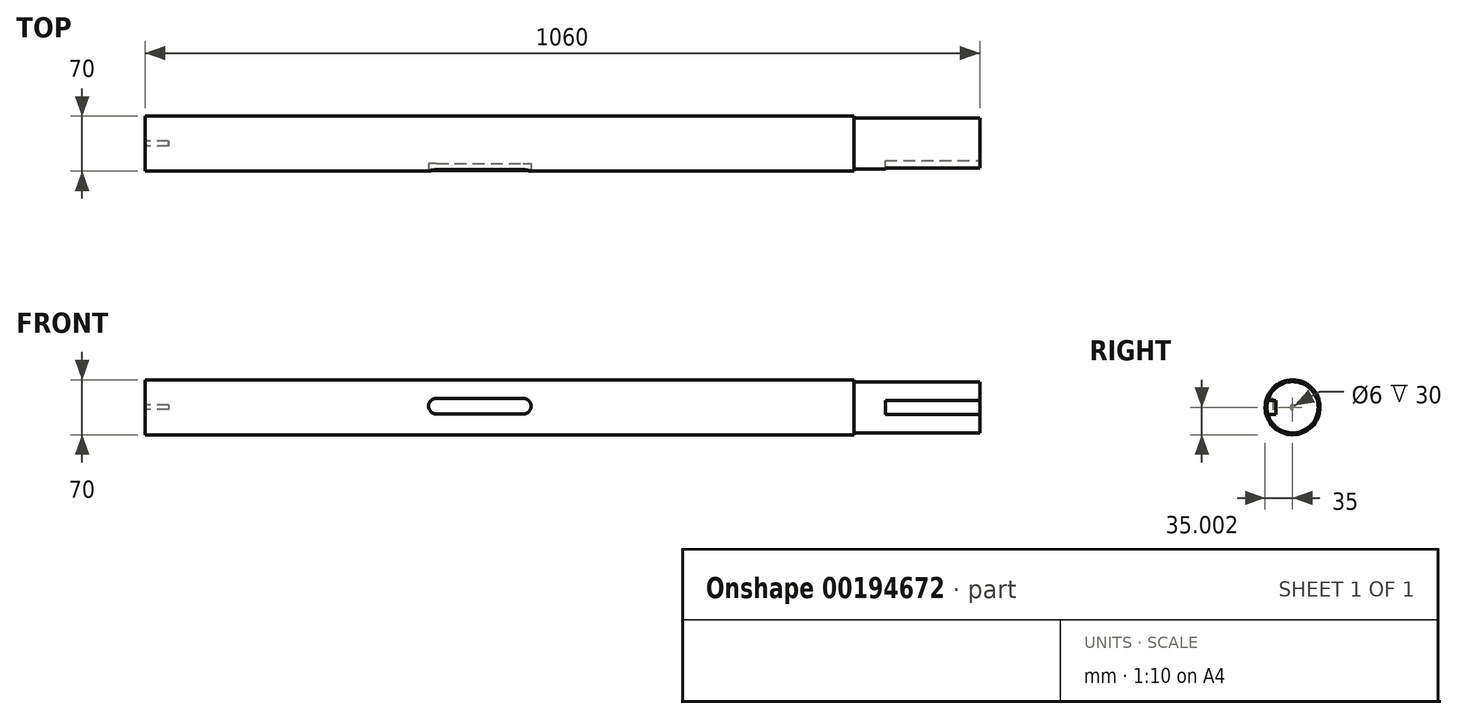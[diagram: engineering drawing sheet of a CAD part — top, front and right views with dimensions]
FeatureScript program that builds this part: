
annotation { "Feature Type Name" : "Feature", "Feature Type Description" : "" }
export const myFeature = defineFeature(function(context is Context, id is Id, definition is map)
    precondition{}
    {
        {
            var Q0;
            Q0=qCreatedBy(makeId("Front.planeOp"),FACE);
            var sketch = newSketch(context, id + "F0", { "sketchPlane" : qUnion([Q0])});
            skLineSegment(sketch, "E0", {"start": v(-663.35, -62.58) * mm, "end": v(236.65, -62.58) * mm});
            skLineSegment(sketch, "E1", {"start": v(236.65, -62.58) * mm, "end": v(236.65, -65.08) * mm});
            skLineSegment(sketch, "E2", {"start": v(236.65, -65.08) * mm, "end": v(396.65, -65.08) * mm});
            skLineSegment(sketch, "E3", {"start": v(396.65, -65.08) * mm, "end": v(396.65, -97.58) * mm});
            skLineSegment(sketch, "E4", {"start": v(396.65, -97.58) * mm, "end": v(-663.35, -97.58) * mm});
            skLineSegment(sketch, "E5", {"start": v(-663.35, -97.58) * mm, "end": v(-663.35, -62.58) * mm});
            skSolve(sketch);
        }
        {
            var Q0;
            Q0=makeQuery(id+"F0.imprint","IMPRINT",FACE,{"disambiguationData":[TD([[makeQuery(id+"F0.imprint","IMPRINT",EDGE,{"derivedFrom":sQuery(id+"F0.wireOp",EDGE,"E0")}),-1.0]])]});
            var Q1;
            Q1=sQuery(id+"F0.wireOp",EDGE,"E4");
            revolve(context, id + "F1", {"entities" : qUnion([Q0]), "axis" : qUnion([Q1]), "revolveType" : RevolveType.FULL});
        }
        {
            var Q0;
            Q0=makeQuery(id+"F1.opRevolve","SWEPT_FACE",FACE,{"disambiguationData":[OSD([sQuery(id+"F0.wireOp",EDGE,"E3")])]});
            var sketch = newSketch(context, id + "F2", { "sketchPlane" : qUnion([Q0])});
            skLineSegment(sketch, "E6", {"start": v(-31.23, -88.58) * mm, "end": v(-21.23, -88.58) * mm});
            skLineSegment(sketch, "E7", {"start": v(-21.23, -88.58) * mm, "end": v(-21.23, -106.58) * mm});
            skLineSegment(sketch, "E8", {"start": v(-21.23, -106.58) * mm, "end": v(-31.23, -106.58) * mm});
            skSolve(sketch);
        }
        {
            var Q0;
            {var subQ0=sQuery(id+"F2.wireOp",EDGE,"E6");Q0=makeQuery(id+"F2.imprint","IMPRINT",FACE,{"disambiguationData":[TD([[makeQuery(id+"F2.imprint","IMPRINT",EDGE,{"derivedFrom":subQ0}),-1.0]])]});}
            extrude(context, id + "F3", {"entities" : qUnion([Q0]), "operationType" : NewBodyOperationType.REMOVE, "oppositeDirection" : true, "depth" : 120 * mm});
        }
        {
            var Q0;
            Q0=qCreatedBy(makeId("Front.planeOp"),FACE);
            cPlane(context, id + "F4", {"entities" : qUnion([Q0]), "cplaneType" : CPlaneType.OFFSET, "offset" : 35 * mm, "width" : 150 * mm, "height" : 150 * mm});
        }
        {
            var Q0;
            Q0=qCreatedBy(id+"F4.planeOp",FACE);
            var sketch = newSketch(context, id + "F5", { "sketchPlane" : qUnion([Q0])});
            skLineSegment(sketch, "E9", {"start": v(-293.35, -86.1) * mm, "end": v(-183.35, -86.1) * mm});
            skLineSegment(sketch, "E10", {"start": v(-183.35, -106.1) * mm, "end": v(-293.35, -106.1) * mm});
            skArc(sketch, "E11", {"start": v(-293.35, -86.1) * mm, "mid": v(-303.35, -96.1) * mm, "end": v(-293.35, -106.1) * mm});
            skArc(sketch, "E12", {"start": v(-183.35, -106.1) * mm, "mid": v(-173.35, -96.1) * mm, "end": v(-183.35, -86.1) * mm});
            skSolve(sketch);
        }
        {
            var Q0;
            Q0=makeQuery(id+"F5.imprint","IMPRINT",FACE,{"disambiguationData":[TD([[makeQuery(id+"F5.imprint","IMPRINT",EDGE,{"derivedFrom":sQuery(id+"F5.wireOp",EDGE,"E9")}),-1.0]])]});
            extrude(context, id + "F6", {"entities" : qUnion([Q0]), "operationType" : NewBodyOperationType.REMOVE, "oppositeDirection" : true, "depth" : 10 * mm});
        }
        {
            var Q0;
            Q0=makeQuery(id+"F1.opRevolve","SWEPT_FACE",FACE,{"disambiguationData":[OSD([sQuery(id+"F0.wireOp",EDGE,"E5")])]});
            var sketch = newSketch(context, id + "F7", { "sketchPlane" : qUnion([Q0])});
            skCircle(sketch, "E13", {"center": v(0, -97.58) * mm, "radius": 3 * mm});
            skSolve(sketch);
        }
        {
            var Q0;
            Q0=makeQuery(id+"F7.imprint","IMPRINT",FACE,{"disambiguationData":[TD([[makeQuery(id+"F7.imprint","IMPRINT",EDGE,{"derivedFrom":sQuery(id+"F7.wireOp",EDGE,"E13")}),1.0]])]});
            extrude(context, id + "F8", {"entities" : qUnion([Q0]), "operationType" : NewBodyOperationType.REMOVE, "oppositeDirection" : true, "depth" : 30 * mm});
        }
    });
